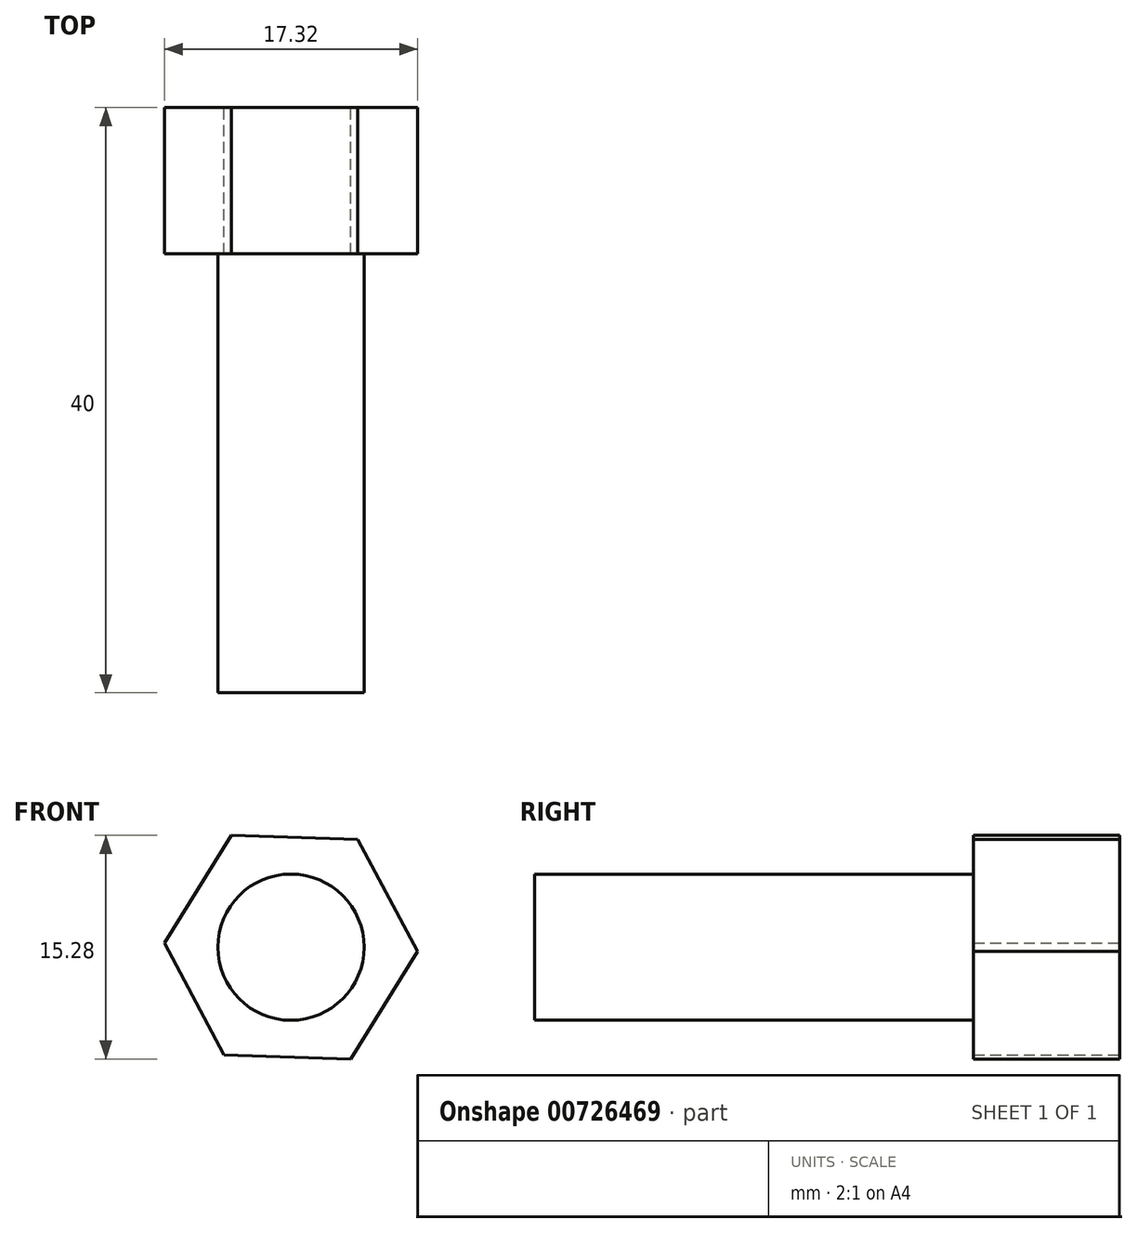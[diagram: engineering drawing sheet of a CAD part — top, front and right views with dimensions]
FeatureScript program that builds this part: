
annotation { "Feature Type Name" : "Feature", "Feature Type Description" : "" }
export const myFeature = defineFeature(function(context is Context, id is Id, definition is map)
    precondition{}
    {
        {
            var Q0;
            Q0=qCreatedBy(makeId("Front.planeOp"),FACE);
            var sketch = newSketch(context, id + "F0", { "sketchPlane" : qUnion([Q0])});
            skCircle(sketch, "E0.cCircle", {"center": v(0, 0) * mm, "radius": 7.5 * mm, "construction": true});
            skLineSegment(sketch, "E0.0", {"start": v(4.57, 7.36) * mm, "end": v(8.66, -0.28) * mm});
            skLineSegment(sketch, "E0.1", {"start": v(8.66, -0.28) * mm, "end": v(4.08, -7.64) * mm});
            skLineSegment(sketch, "E0.2", {"start": v(4.08, -7.64) * mm, "end": v(-4.57, -7.36) * mm});
            skLineSegment(sketch, "E0.3", {"start": v(-4.57, -7.36) * mm, "end": v(-8.66, 0.28) * mm});
            skLineSegment(sketch, "E0.4", {"start": v(-8.66, 0.28) * mm, "end": v(-4.08, 7.64) * mm});
            skLineSegment(sketch, "E0.5", {"start": v(-4.08, 7.64) * mm, "end": v(4.57, 7.36) * mm});
            skPoint(sketch, "E0.0.midPoint", {"position": v(6.61, 3.54) * mm});
            skSolve(sketch);
        }
        {
            var Q0;
            Q0 = qSketchRegion(id + "F0", true);
            extrude(context, id + "F1", {"entities" : qUnion([Q0]), "depth" : 10 * mm, "offsetDistance" : 25 * mm});
        }
        {
            var Q0;
            Q0=makeQuery(id+"F1.opExtrude","CAP_FACE",FACE,{"disambiguationData":[OSD([sQuery(id+"F0.wireOp",EDGE,"E0.0"),sQuery(id+"F0.wireOp",EDGE,"E0.1"),sQuery(id+"F0.wireOp",EDGE,"E0.2"),sQuery(id+"F0.wireOp",EDGE,"E0.3"),sQuery(id+"F0.wireOp",EDGE,"E0.4"),sQuery(id+"F0.wireOp",EDGE,"E0.5")])],"isStart":false});
            var sketch = newSketch(context, id + "F2", { "sketchPlane" : qUnion([Q0])});
            skCircle(sketch, "E1", {"center": v(0, 0) * mm, "radius": 5 * mm});
            skSolve(sketch);
        }
        {
            var Q0;
            Q0=makeQuery(id+"F2.imprint","IMPRINT",FACE,{"disambiguationData":[TD([[makeQuery(id+"F2.imprint","IMPRINT",EDGE,{"derivedFrom":sQuery(id+"F2.wireOp",EDGE,"E1")}),1.0]])]});
            extrude(context, id + "F3", {"entities" : qUnion([Q0]), "operationType" : NewBodyOperationType.ADD, "depth" : 30 * mm, "offsetDistance" : 25 * mm});
        }
    });
